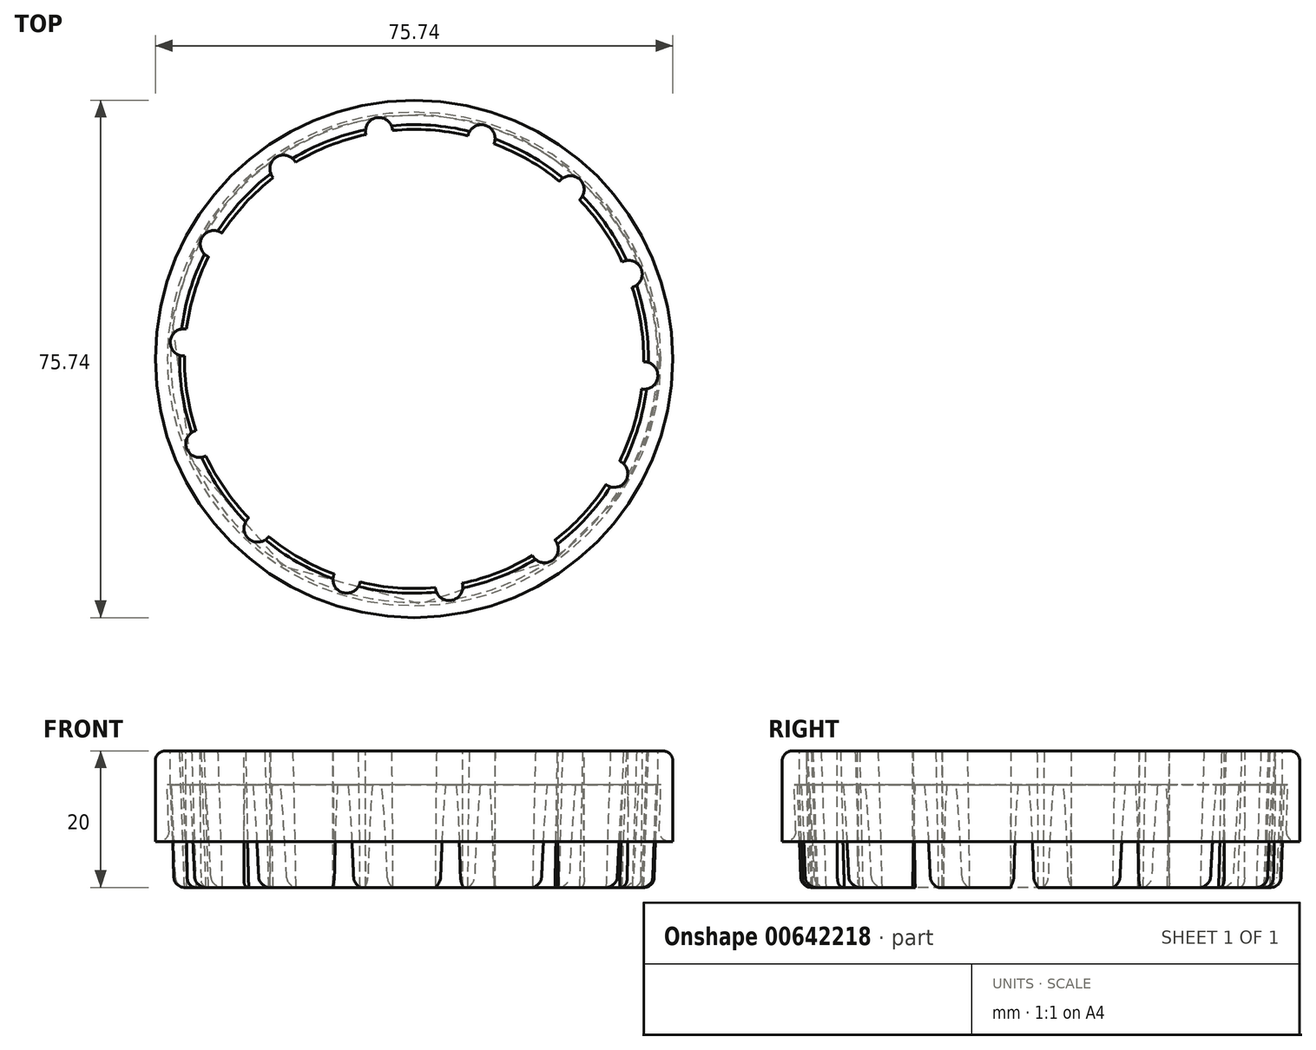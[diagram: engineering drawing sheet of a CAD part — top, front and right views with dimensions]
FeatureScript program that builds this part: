
annotation { "Feature Type Name" : "Feature", "Feature Type Description" : "" }
export const myFeature = defineFeature(function(context is Context, id is Id, definition is map)
    precondition{}
    {
        {
            var Q0;
            Q0=qCreatedBy(makeId("Front.planeOp"),FACE);
            var sketch = newSketch(context, id + "F0", { "sketchPlane" : qUnion([Q0])});
            skLineSegment(sketch, "E0.top", {"start": v(-33.6, 0) * mm, "end": v(-35.1, 0) * mm});
            skLineSegment(sketch, "E1", {"start": v(-35.1, 0) * mm, "end": v(-35.62, 15) * mm});
            skPoint(sketch, "E2.orphan", {"position": v(-35.62, 0) * mm});
            skLineSegment(sketch, "E3.top", {"start": v(-34.3, 20) * mm, "end": v(-37.87, 20) * mm});
            skLineSegment(sketch, "E3.right", {"start": v(-37.87, 15) * mm, "end": v(-37.87, 20) * mm});
            skLineSegment(sketch, "E4", {"start": v(-34.3, 20) * mm, "end": v(-33.6, 0) * mm});
            skLineSegment(sketch, "E5", {"start": v(-36.12, 15) * mm, "end": v(-35.83, 6.78) * mm});
            skLineSegment(sketch, "E6", {"start": v(-37.87, 15) * mm, "end": v(-37.87, 6.71) * mm});
            skLineSegment(sketch, "E7", {"start": v(-35.62, 0) * mm, "end": v(-35.6, 0) * mm});
            skLineSegment(sketch, "E8.trimOffspring", {"start": v(-35.62, 15) * mm, "end": v(-36.12, 15) * mm});
            skPoint(sketch, "E0.left.start.orphan", {"position": v(0, 15) * mm});
            skPoint(sketch, "E9.orphan", {"position": v(0, 0) * mm});
            skLineSegment(sketch, "E10", {"start": v(0, 21.76) * mm, "end": v(0, 0) * mm, "construction": true});
            skLineSegment(sketch, "E11", {"start": v(-35.83, 6.78) * mm, "end": v(-37.87, 6.71) * mm});
            skPoint(sketch, "E12.orphan", {"position": v(-37.87, 0) * mm});
            skSolve(sketch);
        }
        {
            var Q0;
            Q0=makeQuery(id+"F0.imprint","IMPRINT",FACE,{"disambiguationData":[TD([[makeQuery(id+"F0.imprint","IMPRINT",EDGE,{"derivedFrom":sQuery(id+"F0.wireOp",EDGE,"E0.top")}),-1.0]])]});
            var Q1;
            Q1=sQuery(id+"F0.wireOp",EDGE,"E10");
            revolve(context, id + "F1", {"entities" : qUnion([Q0]), "axis" : qUnion([Q1]), "revolveType" : RevolveType.FULL});
        }
        {
            var Q0;
            Q0=makeQuery(id+"F1.opRevolve","SWEPT_FACE",FACE,{"disambiguationData":[OSD([sQuery(id+"F0.wireOp",EDGE,"E3.top")])]});
            var sketch = newSketch(context, id + "F2", { "sketchPlane" : qUnion([Q0])});
            skCircle(sketch, "E13.cCircle", {"center": v(0, 0) * mm, "radius": 32.91 * mm, "construction": true});
            skLineSegment(sketch, "E13.0", {"start": v(-19.1, 27.84) * mm, "end": v(-5.13, 33.37) * mm, "construction": true});
            skLineSegment(sketch, "E13.1", {"start": v(-5.13, 33.37) * mm, "end": v(9.86, 32.29) * mm, "construction": true});
            skLineSegment(sketch, "E13.2", {"start": v(9.86, 32.29) * mm, "end": v(22.9, 24.81) * mm, "construction": true});
            skLineSegment(sketch, "E13.3", {"start": v(22.9, 24.81) * mm, "end": v(31.39, 12.43) * mm, "construction": true});
            skLineSegment(sketch, "E13.4", {"start": v(31.39, 12.43) * mm, "end": v(33.67, -2.42) * mm, "construction": true});
            skLineSegment(sketch, "E13.5", {"start": v(33.67, -2.42) * mm, "end": v(29.29, -16.8) * mm, "construction": true});
            skLineSegment(sketch, "E13.6", {"start": v(29.29, -16.8) * mm, "end": v(19.1, -27.84) * mm, "construction": true});
            skLineSegment(sketch, "E13.7", {"start": v(19.1, -27.84) * mm, "end": v(5.13, -33.37) * mm, "construction": true});
            skLineSegment(sketch, "E13.8", {"start": v(5.13, -33.37) * mm, "end": v(-9.86, -32.29) * mm, "construction": true});
            skLineSegment(sketch, "E13.9", {"start": v(-9.86, -32.29) * mm, "end": v(-22.9, -24.81) * mm, "construction": true});
            skLineSegment(sketch, "E13.10", {"start": v(-22.9, -24.81) * mm, "end": v(-31.39, -12.43) * mm, "construction": true});
            skLineSegment(sketch, "E13.11", {"start": v(-31.39, -12.43) * mm, "end": v(-33.67, 2.42) * mm, "construction": true});
            skLineSegment(sketch, "E13.12", {"start": v(-33.67, 2.42) * mm, "end": v(-29.29, 16.8) * mm, "construction": true});
            skLineSegment(sketch, "E13.13", {"start": v(-29.29, 16.8) * mm, "end": v(-19.1, 27.84) * mm, "construction": true});
            skPoint(sketch, "E13.0.midPoint", {"position": v(-12.11, 30.6) * mm});
            skCircle(sketch, "E14", {"center": v(-5.13, 33.37) * mm, "radius": 1.97 * mm});
            skCircle(sketch, "E15", {"center": v(-19.1, 27.84) * mm, "radius": 2 * mm});
            skCircle(sketch, "E16", {"center": v(-29.29, 16.8) * mm, "radius": 2 * mm});
            skCircle(sketch, "E17", {"center": v(-33.67, 2.42) * mm, "radius": 2 * mm});
            skCircle(sketch, "E18", {"center": v(9.86, 32.29) * mm, "radius": 2 * mm});
            skCircle(sketch, "E19", {"center": v(22.9, 24.81) * mm, "radius": 2 * mm});
            skCircle(sketch, "E20", {"center": v(31.39, 12.43) * mm, "radius": 2 * mm});
            skCircle(sketch, "E21", {"center": v(33.67, -2.42) * mm, "radius": 2 * mm});
            skCircle(sketch, "E22", {"center": v(29.29, -16.8) * mm, "radius": 2 * mm});
            skCircle(sketch, "E23", {"center": v(19.1, -27.84) * mm, "radius": 2 * mm});
            skCircle(sketch, "E24", {"center": v(5.13, -33.37) * mm, "radius": 2 * mm});
            skCircle(sketch, "E25", {"center": v(-9.86, -32.29) * mm, "radius": 2 * mm});
            skCircle(sketch, "E26", {"center": v(-22.9, -24.81) * mm, "radius": 2 * mm});
            skCircle(sketch, "E27", {"center": v(-31.39, -12.43) * mm, "radius": 2 * mm});
            skSolve(sketch);
        }
        {
            var Q0;
            {var subQ0=sQuery(id+"F2.wireOp",EDGE,"E23");var subQ1=makeQuery(id+"F1.opRevolve","SWEPT_EDGE",EDGE,{"disambiguationData":[OSD([sQuery(id+"F0.wireOp",EDGE,"E3.top"),sQuery(id+"F0.wireOp",EDGE,"E4")])]});var subQ2=makeQuery(id+"F2.imprint","INTERSECT",VERTEX,{"disambiguationData":[OD(0.0)],"derivedFrom":[subQ1,subQ0]});Q0=makeQuery(id+"F2.imprint","IMPRINT",FACE,{"disambiguationData":[TD([[makeQuery(id+"F2.imprint","IMPRINT",EDGE,{"disambiguationData":[TD([[subQ2,-1.0]])],"derivedFrom":subQ0}),1.0]])]});}
            var Q1;
            {var subQ0=sQuery(id+"F2.wireOp",EDGE,"E23");var subQ1=makeQuery(id+"F1.opRevolve","SWEPT_EDGE",EDGE,{"disambiguationData":[OSD([sQuery(id+"F0.wireOp",EDGE,"E3.top"),sQuery(id+"F0.wireOp",EDGE,"E4")])]});var subQ2=makeQuery(id+"F2.imprint","INTERSECT",VERTEX,{"disambiguationData":[OD(0.0)],"derivedFrom":[subQ1,subQ0]});Q1=makeQuery(id+"F2.imprint","IMPRINT",FACE,{"disambiguationData":[TD([[makeQuery(id+"F2.imprint","IMPRINT",EDGE,{"disambiguationData":[TD([[subQ2,1.0]])],"derivedFrom":subQ0}),1.0]])]});}
            var Q2;
            {var subQ0=sQuery(id+"F2.wireOp",EDGE,"E22");var subQ1=makeQuery(id+"F1.opRevolve","SWEPT_EDGE",EDGE,{"disambiguationData":[OSD([sQuery(id+"F0.wireOp",EDGE,"E3.top"),sQuery(id+"F0.wireOp",EDGE,"E4")])]});var subQ2=makeQuery(id+"F2.imprint","INTERSECT",VERTEX,{"disambiguationData":[OD(0.0)],"derivedFrom":[subQ1,subQ0]});Q2=makeQuery(id+"F2.imprint","IMPRINT",FACE,{"disambiguationData":[TD([[makeQuery(id+"F2.imprint","IMPRINT",EDGE,{"disambiguationData":[TD([[subQ2,-1.0]])],"derivedFrom":subQ0}),1.0]])]});}
            var Q3;
            {var subQ0=sQuery(id+"F2.wireOp",EDGE,"E21");var subQ1=makeQuery(id+"F1.opRevolve","SWEPT_EDGE",EDGE,{"disambiguationData":[OSD([sQuery(id+"F0.wireOp",EDGE,"E3.top"),sQuery(id+"F0.wireOp",EDGE,"E4")])]});var subQ2=makeQuery(id+"F2.imprint","INTERSECT",VERTEX,{"disambiguationData":[OD(0.0)],"derivedFrom":[subQ1,subQ0]});Q3=makeQuery(id+"F2.imprint","IMPRINT",FACE,{"disambiguationData":[TD([[makeQuery(id+"F2.imprint","IMPRINT",EDGE,{"disambiguationData":[TD([[subQ2,-1.0]])],"derivedFrom":subQ0}),1.0]])]});}
            var Q4;
            {var subQ0=sQuery(id+"F2.wireOp",EDGE,"E20");var subQ1=makeQuery(id+"F1.opRevolve","SWEPT_EDGE",EDGE,{"disambiguationData":[OSD([sQuery(id+"F0.wireOp",EDGE,"E3.top"),sQuery(id+"F0.wireOp",EDGE,"E4")])]});var subQ2=makeQuery(id+"F2.imprint","INTERSECT",VERTEX,{"disambiguationData":[OD(0.0)],"derivedFrom":[subQ1,subQ0]});Q4=makeQuery(id+"F2.imprint","IMPRINT",FACE,{"disambiguationData":[TD([[makeQuery(id+"F2.imprint","IMPRINT",EDGE,{"disambiguationData":[TD([[subQ2,-1.0]])],"derivedFrom":subQ0}),1.0]])]});}
            var Q5;
            {var subQ0=sQuery(id+"F2.wireOp",EDGE,"E20");var subQ1=makeQuery(id+"F1.opRevolve","SWEPT_EDGE",EDGE,{"disambiguationData":[OSD([sQuery(id+"F0.wireOp",EDGE,"E3.top"),sQuery(id+"F0.wireOp",EDGE,"E4")])]});var subQ2=makeQuery(id+"F2.imprint","INTERSECT",VERTEX,{"disambiguationData":[OD(0.0)],"derivedFrom":[subQ1,subQ0]});Q5=makeQuery(id+"F2.imprint","IMPRINT",FACE,{"disambiguationData":[TD([[makeQuery(id+"F2.imprint","IMPRINT",EDGE,{"disambiguationData":[TD([[subQ2,1.0]])],"derivedFrom":subQ0}),1.0]])]});}
            var Q6;
            {var subQ0=sQuery(id+"F2.wireOp",EDGE,"E21");var subQ1=makeQuery(id+"F1.opRevolve","SWEPT_EDGE",EDGE,{"disambiguationData":[OSD([sQuery(id+"F0.wireOp",EDGE,"E3.top"),sQuery(id+"F0.wireOp",EDGE,"E4")])]});var subQ2=makeQuery(id+"F2.imprint","INTERSECT",VERTEX,{"disambiguationData":[OD(0.0)],"derivedFrom":[subQ1,subQ0]});Q6=makeQuery(id+"F2.imprint","IMPRINT",FACE,{"disambiguationData":[TD([[makeQuery(id+"F2.imprint","IMPRINT",EDGE,{"disambiguationData":[TD([[subQ2,1.0]])],"derivedFrom":subQ0}),1.0]])]});}
            var Q7;
            {var subQ0=sQuery(id+"F2.wireOp",EDGE,"E19");var subQ1=makeQuery(id+"F1.opRevolve","SWEPT_EDGE",EDGE,{"disambiguationData":[OSD([sQuery(id+"F0.wireOp",EDGE,"E3.top"),sQuery(id+"F0.wireOp",EDGE,"E4")])]});var subQ2=makeQuery(id+"F2.imprint","INTERSECT",VERTEX,{"disambiguationData":[OD(0.0)],"derivedFrom":[subQ1,subQ0]});Q7=makeQuery(id+"F2.imprint","IMPRINT",FACE,{"disambiguationData":[TD([[makeQuery(id+"F2.imprint","IMPRINT",EDGE,{"disambiguationData":[TD([[subQ2,1.0]])],"derivedFrom":subQ0}),1.0]])]});}
            var Q8;
            {var subQ0=sQuery(id+"F2.wireOp",EDGE,"E18");var subQ1=makeQuery(id+"F1.opRevolve","SWEPT_EDGE",EDGE,{"disambiguationData":[OSD([sQuery(id+"F0.wireOp",EDGE,"E3.top"),sQuery(id+"F0.wireOp",EDGE,"E4")])]});var subQ2=makeQuery(id+"F2.imprint","INTERSECT",VERTEX,{"disambiguationData":[OD(0.0)],"derivedFrom":[subQ1,subQ0]});Q8=makeQuery(id+"F2.imprint","IMPRINT",FACE,{"disambiguationData":[TD([[makeQuery(id+"F2.imprint","IMPRINT",EDGE,{"disambiguationData":[TD([[subQ2,1.0]])],"derivedFrom":subQ0}),1.0]])]});}
            var Q9;
            {var subQ0=sQuery(id+"F2.wireOp",EDGE,"E18");var subQ1=makeQuery(id+"F1.opRevolve","SWEPT_EDGE",EDGE,{"disambiguationData":[OSD([sQuery(id+"F0.wireOp",EDGE,"E3.top"),sQuery(id+"F0.wireOp",EDGE,"E4")])]});var subQ2=makeQuery(id+"F2.imprint","INTERSECT",VERTEX,{"disambiguationData":[OD(0.0)],"derivedFrom":[subQ1,subQ0]});Q9=makeQuery(id+"F2.imprint","IMPRINT",FACE,{"disambiguationData":[TD([[makeQuery(id+"F2.imprint","IMPRINT",EDGE,{"disambiguationData":[TD([[subQ2,-1.0]])],"derivedFrom":subQ0}),1.0]])]});}
            var Q10;
            {var subQ0=sQuery(id+"F2.wireOp",EDGE,"E14");var subQ1=makeQuery(id+"F1.opRevolve","SWEPT_EDGE",EDGE,{"disambiguationData":[OSD([sQuery(id+"F0.wireOp",EDGE,"E3.top"),sQuery(id+"F0.wireOp",EDGE,"E4")])]});var subQ2=makeQuery(id+"F2.imprint","INTERSECT",VERTEX,{"disambiguationData":[OD(0.0)],"derivedFrom":[subQ1,subQ0]});Q10=makeQuery(id+"F2.imprint","IMPRINT",FACE,{"disambiguationData":[TD([[makeQuery(id+"F2.imprint","IMPRINT",EDGE,{"disambiguationData":[TD([[subQ2,1.0]])],"derivedFrom":subQ0}),1.0]])]});}
            var Q11;
            {var subQ0=sQuery(id+"F2.wireOp",EDGE,"E15");var subQ1=makeQuery(id+"F1.opRevolve","SWEPT_EDGE",EDGE,{"disambiguationData":[OSD([sQuery(id+"F0.wireOp",EDGE,"E3.top"),sQuery(id+"F0.wireOp",EDGE,"E4")])]});var subQ2=makeQuery(id+"F2.imprint","INTERSECT",VERTEX,{"disambiguationData":[OD(0.0)],"derivedFrom":[subQ1,subQ0]});Q11=makeQuery(id+"F2.imprint","IMPRINT",FACE,{"disambiguationData":[TD([[makeQuery(id+"F2.imprint","IMPRINT",EDGE,{"disambiguationData":[TD([[subQ2,1.0]])],"derivedFrom":subQ0}),1.0]])]});}
            var Q12;
            {var subQ0=sQuery(id+"F2.wireOp",EDGE,"E16");var subQ1=makeQuery(id+"F1.opRevolve","SWEPT_EDGE",EDGE,{"disambiguationData":[OSD([sQuery(id+"F0.wireOp",EDGE,"E3.top"),sQuery(id+"F0.wireOp",EDGE,"E4")])]});var subQ2=makeQuery(id+"F2.imprint","INTERSECT",VERTEX,{"disambiguationData":[OD(0.0)],"derivedFrom":[subQ1,subQ0]});Q12=makeQuery(id+"F2.imprint","IMPRINT",FACE,{"disambiguationData":[TD([[makeQuery(id+"F2.imprint","IMPRINT",EDGE,{"disambiguationData":[TD([[subQ2,1.0]])],"derivedFrom":subQ0}),1.0]])]});}
            var Q13;
            {var subQ0=sQuery(id+"F2.wireOp",EDGE,"E17");var subQ1=makeQuery(id+"F1.opRevolve","SWEPT_EDGE",EDGE,{"disambiguationData":[OSD([sQuery(id+"F0.wireOp",EDGE,"E3.top"),sQuery(id+"F0.wireOp",EDGE,"E4")])]});var subQ2=makeQuery(id+"F2.imprint","INTERSECT",VERTEX,{"disambiguationData":[OD(0.0)],"derivedFrom":[subQ1,subQ0]});Q13=makeQuery(id+"F2.imprint","IMPRINT",FACE,{"disambiguationData":[TD([[makeQuery(id+"F2.imprint","IMPRINT",EDGE,{"disambiguationData":[TD([[subQ2,1.0]])],"derivedFrom":subQ0}),1.0]])]});}
            var Q14;
            {var subQ0=sQuery(id+"F2.wireOp",EDGE,"E24");var subQ1=makeQuery(id+"F1.opRevolve","SWEPT_EDGE",EDGE,{"disambiguationData":[OSD([sQuery(id+"F0.wireOp",EDGE,"E3.top"),sQuery(id+"F0.wireOp",EDGE,"E4")])]});var subQ2=makeQuery(id+"F2.imprint","INTERSECT",VERTEX,{"disambiguationData":[OD(0.0)],"derivedFrom":[subQ1,subQ0]});Q14=makeQuery(id+"F2.imprint","IMPRINT",FACE,{"disambiguationData":[TD([[makeQuery(id+"F2.imprint","IMPRINT",EDGE,{"disambiguationData":[TD([[subQ2,-1.0]])],"derivedFrom":subQ0}),1.0]])]});}
            var Q15;
            {var subQ0=sQuery(id+"F2.wireOp",EDGE,"E24");var subQ1=makeQuery(id+"F1.opRevolve","SWEPT_EDGE",EDGE,{"disambiguationData":[OSD([sQuery(id+"F0.wireOp",EDGE,"E3.top"),sQuery(id+"F0.wireOp",EDGE,"E4")])]});var subQ2=makeQuery(id+"F2.imprint","INTERSECT",VERTEX,{"disambiguationData":[OD(0.0)],"derivedFrom":[subQ1,subQ0]});Q15=makeQuery(id+"F2.imprint","IMPRINT",FACE,{"disambiguationData":[TD([[makeQuery(id+"F2.imprint","IMPRINT",EDGE,{"disambiguationData":[TD([[subQ2,1.0]])],"derivedFrom":subQ0}),1.0]])]});}
            var Q16;
            {var subQ0=sQuery(id+"F2.wireOp",EDGE,"E19");var subQ1=makeQuery(id+"F1.opRevolve","SWEPT_EDGE",EDGE,{"disambiguationData":[OSD([sQuery(id+"F0.wireOp",EDGE,"E3.top"),sQuery(id+"F0.wireOp",EDGE,"E4")])]});var subQ2=makeQuery(id+"F2.imprint","INTERSECT",VERTEX,{"disambiguationData":[OD(0.0)],"derivedFrom":[subQ1,subQ0]});Q16=makeQuery(id+"F2.imprint","IMPRINT",FACE,{"disambiguationData":[TD([[makeQuery(id+"F2.imprint","IMPRINT",EDGE,{"disambiguationData":[TD([[subQ2,-1.0]])],"derivedFrom":subQ0}),1.0]])]});}
            var Q17;
            {var subQ0=sQuery(id+"F2.wireOp",EDGE,"E14");var subQ1=makeQuery(id+"F1.opRevolve","SWEPT_EDGE",EDGE,{"disambiguationData":[OSD([sQuery(id+"F0.wireOp",EDGE,"E3.top"),sQuery(id+"F0.wireOp",EDGE,"E4")])]});var subQ2=makeQuery(id+"F2.imprint","INTERSECT",VERTEX,{"disambiguationData":[OD(0.0)],"derivedFrom":[subQ1,subQ0]});Q17=makeQuery(id+"F2.imprint","IMPRINT",FACE,{"disambiguationData":[TD([[makeQuery(id+"F2.imprint","IMPRINT",EDGE,{"disambiguationData":[TD([[subQ2,-1.0]])],"derivedFrom":subQ0}),1.0]])]});}
            var Q18;
            {var subQ0=sQuery(id+"F2.wireOp",EDGE,"E15");var subQ1=makeQuery(id+"F1.opRevolve","SWEPT_EDGE",EDGE,{"disambiguationData":[OSD([sQuery(id+"F0.wireOp",EDGE,"E3.top"),sQuery(id+"F0.wireOp",EDGE,"E4")])]});var subQ2=makeQuery(id+"F2.imprint","INTERSECT",VERTEX,{"disambiguationData":[OD(0.0)],"derivedFrom":[subQ1,subQ0]});Q18=makeQuery(id+"F2.imprint","IMPRINT",FACE,{"disambiguationData":[TD([[makeQuery(id+"F2.imprint","IMPRINT",EDGE,{"disambiguationData":[TD([[subQ2,-1.0]])],"derivedFrom":subQ0}),1.0]])]});}
            var Q19;
            {var subQ0=sQuery(id+"F2.wireOp",EDGE,"E16");var subQ1=makeQuery(id+"F1.opRevolve","SWEPT_EDGE",EDGE,{"disambiguationData":[OSD([sQuery(id+"F0.wireOp",EDGE,"E3.top"),sQuery(id+"F0.wireOp",EDGE,"E4")])]});var subQ2=makeQuery(id+"F2.imprint","INTERSECT",VERTEX,{"disambiguationData":[OD(0.0)],"derivedFrom":[subQ1,subQ0]});Q19=makeQuery(id+"F2.imprint","IMPRINT",FACE,{"disambiguationData":[TD([[makeQuery(id+"F2.imprint","IMPRINT",EDGE,{"disambiguationData":[TD([[subQ2,-1.0]])],"derivedFrom":subQ0}),1.0]])]});}
            var Q20;
            {var subQ0=sQuery(id+"F2.wireOp",EDGE,"E22");var subQ1=makeQuery(id+"F1.opRevolve","SWEPT_EDGE",EDGE,{"disambiguationData":[OSD([sQuery(id+"F0.wireOp",EDGE,"E3.top"),sQuery(id+"F0.wireOp",EDGE,"E4")])]});var subQ2=makeQuery(id+"F2.imprint","INTERSECT",VERTEX,{"disambiguationData":[OD(0.0)],"derivedFrom":[subQ1,subQ0]});Q20=makeQuery(id+"F2.imprint","IMPRINT",FACE,{"disambiguationData":[TD([[makeQuery(id+"F2.imprint","IMPRINT",EDGE,{"disambiguationData":[TD([[subQ2,1.0]])],"derivedFrom":subQ0}),1.0]])]});}
            var Q21;
            {var subQ0=sQuery(id+"F2.wireOp",EDGE,"E25");var subQ1=makeQuery(id+"F1.opRevolve","SWEPT_EDGE",EDGE,{"disambiguationData":[OSD([sQuery(id+"F0.wireOp",EDGE,"E3.top"),sQuery(id+"F0.wireOp",EDGE,"E4")])]});var subQ2=makeQuery(id+"F2.imprint","INTERSECT",VERTEX,{"disambiguationData":[OD(0.0)],"derivedFrom":[subQ1,subQ0]});Q21=makeQuery(id+"F2.imprint","IMPRINT",FACE,{"disambiguationData":[TD([[makeQuery(id+"F2.imprint","IMPRINT",EDGE,{"disambiguationData":[TD([[subQ2,-1.0]])],"derivedFrom":subQ0}),1.0]])]});}
            var Q22;
            {var subQ0=sQuery(id+"F2.wireOp",EDGE,"E26");var subQ1=makeQuery(id+"F1.opRevolve","SWEPT_EDGE",EDGE,{"disambiguationData":[OSD([sQuery(id+"F0.wireOp",EDGE,"E3.top"),sQuery(id+"F0.wireOp",EDGE,"E4")])]});var subQ2=makeQuery(id+"F2.imprint","INTERSECT",VERTEX,{"disambiguationData":[OD(0.0)],"derivedFrom":[subQ1,subQ0]});Q22=makeQuery(id+"F2.imprint","IMPRINT",FACE,{"disambiguationData":[TD([[makeQuery(id+"F2.imprint","IMPRINT",EDGE,{"disambiguationData":[TD([[subQ2,-1.0]])],"derivedFrom":subQ0}),1.0]])]});}
            var Q23;
            {var subQ0=sQuery(id+"F2.wireOp",EDGE,"E27");var subQ1=makeQuery(id+"F1.opRevolve","SWEPT_EDGE",EDGE,{"disambiguationData":[OSD([sQuery(id+"F0.wireOp",EDGE,"E3.top"),sQuery(id+"F0.wireOp",EDGE,"E4")])]});var subQ2=makeQuery(id+"F2.imprint","INTERSECT",VERTEX,{"disambiguationData":[OD(0.0)],"derivedFrom":[subQ1,subQ0]});Q23=makeQuery(id+"F2.imprint","IMPRINT",FACE,{"disambiguationData":[TD([[makeQuery(id+"F2.imprint","IMPRINT",EDGE,{"disambiguationData":[TD([[subQ2,1.0]])],"derivedFrom":subQ0}),1.0]])]});}
            var Q24;
            {var subQ0=sQuery(id+"F2.wireOp",EDGE,"E26");var subQ1=makeQuery(id+"F1.opRevolve","SWEPT_EDGE",EDGE,{"disambiguationData":[OSD([sQuery(id+"F0.wireOp",EDGE,"E3.top"),sQuery(id+"F0.wireOp",EDGE,"E4")])]});var subQ2=makeQuery(id+"F2.imprint","INTERSECT",VERTEX,{"disambiguationData":[OD(0.0)],"derivedFrom":[subQ1,subQ0]});Q24=makeQuery(id+"F2.imprint","IMPRINT",FACE,{"disambiguationData":[TD([[makeQuery(id+"F2.imprint","IMPRINT",EDGE,{"disambiguationData":[TD([[subQ2,1.0]])],"derivedFrom":subQ0}),1.0]])]});}
            var Q25;
            {var subQ0=sQuery(id+"F2.wireOp",EDGE,"E25");var subQ1=makeQuery(id+"F1.opRevolve","SWEPT_EDGE",EDGE,{"disambiguationData":[OSD([sQuery(id+"F0.wireOp",EDGE,"E3.top"),sQuery(id+"F0.wireOp",EDGE,"E4")])]});var subQ2=makeQuery(id+"F2.imprint","INTERSECT",VERTEX,{"disambiguationData":[OD(0.0)],"derivedFrom":[subQ1,subQ0]});Q25=makeQuery(id+"F2.imprint","IMPRINT",FACE,{"disambiguationData":[TD([[makeQuery(id+"F2.imprint","IMPRINT",EDGE,{"disambiguationData":[TD([[subQ2,1.0]])],"derivedFrom":subQ0}),1.0]])]});}
            var Q26;
            {var subQ0=sQuery(id+"F2.wireOp",EDGE,"E27");var subQ1=makeQuery(id+"F1.opRevolve","SWEPT_EDGE",EDGE,{"disambiguationData":[OSD([sQuery(id+"F0.wireOp",EDGE,"E3.top"),sQuery(id+"F0.wireOp",EDGE,"E4")])]});var subQ2=makeQuery(id+"F2.imprint","INTERSECT",VERTEX,{"disambiguationData":[OD(0.0)],"derivedFrom":[subQ1,subQ0]});Q26=makeQuery(id+"F2.imprint","IMPRINT",FACE,{"disambiguationData":[TD([[makeQuery(id+"F2.imprint","IMPRINT",EDGE,{"disambiguationData":[TD([[subQ2,-1.0]])],"derivedFrom":subQ0}),1.0]])]});}
            var Q27;
            {var subQ0=sQuery(id+"F2.wireOp",EDGE,"E17");var subQ1=makeQuery(id+"F1.opRevolve","SWEPT_EDGE",EDGE,{"disambiguationData":[OSD([sQuery(id+"F0.wireOp",EDGE,"E3.top"),sQuery(id+"F0.wireOp",EDGE,"E4")])]});var subQ2=makeQuery(id+"F2.imprint","INTERSECT",VERTEX,{"disambiguationData":[OD(0.0)],"derivedFrom":[subQ1,subQ0]});Q27=makeQuery(id+"F2.imprint","IMPRINT",FACE,{"disambiguationData":[TD([[makeQuery(id+"F2.imprint","IMPRINT",EDGE,{"disambiguationData":[TD([[subQ2,-1.0]])],"derivedFrom":subQ0}),1.0]])]});}
            extrude(context, id + "F3", {"entities" : qUnion([Q0, Q1, Q2, Q3, Q4, Q5, Q6, Q7, Q8, Q9, Q10, Q11, Q12, Q13, Q14, Q15, Q16, Q17, Q18, Q19, Q20, Q21, Q22, Q23, Q24, Q25, Q26, Q27]), "operationType" : NewBodyOperationType.REMOVE, "oppositeDirection" : true, "depth" : 25 * mm, "offsetDistance" : 25 * mm});
        }
        {
            var Q0;
            {var subQ0=sQuery(id+"F0.wireOp",EDGE,"E0.top");var subQ1=sQuery(id+"F0.wireOp",EDGE,"E1");Q0=makeQuery(id+"F3.boolean.opBoolean","SPLIT",EDGE,{"disambiguationData":[TD([makeQuery(id+"F1.opRevolve","SWEPT_FACE",FACE,{"disambiguationData":[OSD([subQ0])]}),makeQuery(id+"F1.opRevolve","SWEPT_FACE",FACE,{"disambiguationData":[OSD([subQ1])]}),makeQuery(id+"F3.opExtrude","SWEPT_FACE",FACE,{"disambiguationData":[OSD([sQuery(id+"F2.wireOp",EDGE,"E26")])]}),makeQuery(id+"F3.opExtrude","SWEPT_FACE",FACE,{"disambiguationData":[OSD([sQuery(id+"F2.wireOp",EDGE,"E27")])]})])],"derivedFrom":makeQuery(id+"F1.opRevolve","SWEPT_EDGE",EDGE,{"disambiguationData":[OSD([subQ0,subQ1])]})});}
            var Q1;
            {var subQ0=sQuery(id+"F0.wireOp",EDGE,"E0.top");var subQ1=sQuery(id+"F0.wireOp",EDGE,"E1");Q1=makeQuery(id+"F3.boolean.opBoolean","SPLIT",EDGE,{"disambiguationData":[TD([makeQuery(id+"F1.opRevolve","SWEPT_FACE",FACE,{"disambiguationData":[OSD([subQ0])]}),makeQuery(id+"F1.opRevolve","SWEPT_FACE",FACE,{"disambiguationData":[OSD([subQ1])]}),makeQuery(id+"F3.opExtrude","SWEPT_FACE",FACE,{"disambiguationData":[OSD([sQuery(id+"F2.wireOp",EDGE,"E25")])]}),makeQuery(id+"F3.opExtrude","SWEPT_FACE",FACE,{"disambiguationData":[OSD([sQuery(id+"F2.wireOp",EDGE,"E26")])]})])],"derivedFrom":makeQuery(id+"F1.opRevolve","SWEPT_EDGE",EDGE,{"disambiguationData":[OSD([subQ0,subQ1])]})});}
            var Q2;
            {var subQ0=sQuery(id+"F0.wireOp",EDGE,"E0.top");var subQ1=sQuery(id+"F0.wireOp",EDGE,"E1");Q2=makeQuery(id+"F3.boolean.opBoolean","SPLIT",EDGE,{"disambiguationData":[TD([makeQuery(id+"F1.opRevolve","SWEPT_FACE",FACE,{"disambiguationData":[OSD([subQ0])]}),makeQuery(id+"F1.opRevolve","SWEPT_FACE",FACE,{"disambiguationData":[OSD([subQ1])]}),makeQuery(id+"F3.opExtrude","SWEPT_FACE",FACE,{"disambiguationData":[OSD([sQuery(id+"F2.wireOp",EDGE,"E24")])]}),makeQuery(id+"F3.opExtrude","SWEPT_FACE",FACE,{"disambiguationData":[OSD([sQuery(id+"F2.wireOp",EDGE,"E25")])]})])],"derivedFrom":makeQuery(id+"F1.opRevolve","SWEPT_EDGE",EDGE,{"disambiguationData":[OSD([subQ0,subQ1])]})});}
            var Q3;
            {var subQ0=sQuery(id+"F0.wireOp",EDGE,"E0.top");var subQ1=sQuery(id+"F0.wireOp",EDGE,"E1");Q3=makeQuery(id+"F3.boolean.opBoolean","SPLIT",EDGE,{"disambiguationData":[TD([makeQuery(id+"F1.opRevolve","SWEPT_FACE",FACE,{"disambiguationData":[OSD([subQ0])]}),makeQuery(id+"F1.opRevolve","SWEPT_FACE",FACE,{"disambiguationData":[OSD([subQ1])]}),makeQuery(id+"F3.opExtrude","SWEPT_FACE",FACE,{"disambiguationData":[OSD([sQuery(id+"F2.wireOp",EDGE,"E23")])]}),makeQuery(id+"F3.opExtrude","SWEPT_FACE",FACE,{"disambiguationData":[OSD([sQuery(id+"F2.wireOp",EDGE,"E24")])]})])],"derivedFrom":makeQuery(id+"F1.opRevolve","SWEPT_EDGE",EDGE,{"disambiguationData":[OSD([subQ0,subQ1])]})});}
            var Q4;
            {var subQ0=sQuery(id+"F0.wireOp",EDGE,"E0.top");var subQ1=sQuery(id+"F0.wireOp",EDGE,"E1");Q4=makeQuery(id+"F3.boolean.opBoolean","SPLIT",EDGE,{"disambiguationData":[TD([makeQuery(id+"F1.opRevolve","SWEPT_FACE",FACE,{"disambiguationData":[OSD([subQ0])]}),makeQuery(id+"F1.opRevolve","SWEPT_FACE",FACE,{"disambiguationData":[OSD([subQ1])]}),makeQuery(id+"F3.opExtrude","SWEPT_FACE",FACE,{"disambiguationData":[OSD([sQuery(id+"F2.wireOp",EDGE,"E22")])]}),makeQuery(id+"F3.opExtrude","SWEPT_FACE",FACE,{"disambiguationData":[OSD([sQuery(id+"F2.wireOp",EDGE,"E23")])]})])],"derivedFrom":makeQuery(id+"F1.opRevolve","SWEPT_EDGE",EDGE,{"disambiguationData":[OSD([subQ0,subQ1])]})});}
            var Q5;
            {var subQ0=sQuery(id+"F0.wireOp",EDGE,"E0.top");var subQ1=sQuery(id+"F0.wireOp",EDGE,"E1");Q5=makeQuery(id+"F3.boolean.opBoolean","SPLIT",EDGE,{"disambiguationData":[TD([makeQuery(id+"F1.opRevolve","SWEPT_FACE",FACE,{"disambiguationData":[OSD([subQ0])]}),makeQuery(id+"F1.opRevolve","SWEPT_FACE",FACE,{"disambiguationData":[OSD([subQ1])]}),makeQuery(id+"F3.opExtrude","SWEPT_FACE",FACE,{"disambiguationData":[OSD([sQuery(id+"F2.wireOp",EDGE,"E21")])]}),makeQuery(id+"F3.opExtrude","SWEPT_FACE",FACE,{"disambiguationData":[OSD([sQuery(id+"F2.wireOp",EDGE,"E22")])]})])],"derivedFrom":makeQuery(id+"F1.opRevolve","SWEPT_EDGE",EDGE,{"disambiguationData":[OSD([subQ0,subQ1])]})});}
            var Q6;
            {var subQ0=sQuery(id+"F0.wireOp",EDGE,"E0.top");var subQ1=sQuery(id+"F0.wireOp",EDGE,"E1");Q6=makeQuery(id+"F3.boolean.opBoolean","SPLIT",EDGE,{"disambiguationData":[TD([makeQuery(id+"F1.opRevolve","SWEPT_FACE",FACE,{"disambiguationData":[OSD([subQ0])]}),makeQuery(id+"F1.opRevolve","SWEPT_FACE",FACE,{"disambiguationData":[OSD([subQ1])]}),makeQuery(id+"F3.opExtrude","SWEPT_FACE",FACE,{"disambiguationData":[OSD([sQuery(id+"F2.wireOp",EDGE,"E20")])]}),makeQuery(id+"F3.opExtrude","SWEPT_FACE",FACE,{"disambiguationData":[OSD([sQuery(id+"F2.wireOp",EDGE,"E21")])]})])],"derivedFrom":makeQuery(id+"F1.opRevolve","SWEPT_EDGE",EDGE,{"disambiguationData":[OSD([subQ0,subQ1])]})});}
            var Q7;
            {var subQ0=sQuery(id+"F0.wireOp",EDGE,"E0.top");var subQ1=sQuery(id+"F0.wireOp",EDGE,"E1");Q7=makeQuery(id+"F3.boolean.opBoolean","SPLIT",EDGE,{"disambiguationData":[TD([makeQuery(id+"F1.opRevolve","SWEPT_FACE",FACE,{"disambiguationData":[OSD([subQ0])]}),makeQuery(id+"F1.opRevolve","SWEPT_FACE",FACE,{"disambiguationData":[OSD([subQ1])]}),makeQuery(id+"F3.opExtrude","SWEPT_FACE",FACE,{"disambiguationData":[OSD([sQuery(id+"F2.wireOp",EDGE,"E19")])]}),makeQuery(id+"F3.opExtrude","SWEPT_FACE",FACE,{"disambiguationData":[OSD([sQuery(id+"F2.wireOp",EDGE,"E20")])]})])],"derivedFrom":makeQuery(id+"F1.opRevolve","SWEPT_EDGE",EDGE,{"disambiguationData":[OSD([subQ0,subQ1])]})});}
            var Q8;
            {var subQ0=sQuery(id+"F0.wireOp",EDGE,"E0.top");var subQ1=sQuery(id+"F0.wireOp",EDGE,"E1");Q8=makeQuery(id+"F3.boolean.opBoolean","SPLIT",EDGE,{"disambiguationData":[TD([makeQuery(id+"F1.opRevolve","SWEPT_FACE",FACE,{"disambiguationData":[OSD([subQ0])]}),makeQuery(id+"F1.opRevolve","SWEPT_FACE",FACE,{"disambiguationData":[OSD([subQ1])]}),makeQuery(id+"F3.opExtrude","SWEPT_FACE",FACE,{"disambiguationData":[OSD([sQuery(id+"F2.wireOp",EDGE,"E18")])]}),makeQuery(id+"F3.opExtrude","SWEPT_FACE",FACE,{"disambiguationData":[OSD([sQuery(id+"F2.wireOp",EDGE,"E19")])]})])],"derivedFrom":makeQuery(id+"F1.opRevolve","SWEPT_EDGE",EDGE,{"disambiguationData":[OSD([subQ0,subQ1])]})});}
            var Q9;
            {var subQ0=sQuery(id+"F0.wireOp",EDGE,"E0.top");var subQ1=sQuery(id+"F0.wireOp",EDGE,"E1");Q9=makeQuery(id+"F3.boolean.opBoolean","SPLIT",EDGE,{"disambiguationData":[TD([makeQuery(id+"F1.opRevolve","SWEPT_FACE",FACE,{"disambiguationData":[OSD([subQ0])]}),makeQuery(id+"F1.opRevolve","SWEPT_FACE",FACE,{"disambiguationData":[OSD([subQ1])]}),makeQuery(id+"F3.opExtrude","SWEPT_FACE",FACE,{"disambiguationData":[OSD([sQuery(id+"F2.wireOp",EDGE,"E14")])]}),makeQuery(id+"F3.opExtrude","SWEPT_FACE",FACE,{"disambiguationData":[OSD([sQuery(id+"F2.wireOp",EDGE,"E18")])]})])],"derivedFrom":makeQuery(id+"F1.opRevolve","SWEPT_EDGE",EDGE,{"disambiguationData":[OSD([subQ0,subQ1])]})});}
            var Q10;
            {var subQ0=sQuery(id+"F0.wireOp",EDGE,"E0.top");var subQ1=sQuery(id+"F0.wireOp",EDGE,"E1");Q10=makeQuery(id+"F3.boolean.opBoolean","SPLIT",EDGE,{"disambiguationData":[TD([makeQuery(id+"F1.opRevolve","SWEPT_FACE",FACE,{"disambiguationData":[OSD([subQ0])]}),makeQuery(id+"F1.opRevolve","SWEPT_FACE",FACE,{"disambiguationData":[OSD([subQ1])]}),makeQuery(id+"F3.opExtrude","SWEPT_FACE",FACE,{"disambiguationData":[OSD([sQuery(id+"F2.wireOp",EDGE,"E14")])]}),makeQuery(id+"F3.opExtrude","SWEPT_FACE",FACE,{"disambiguationData":[OSD([sQuery(id+"F2.wireOp",EDGE,"E15")])]})])],"derivedFrom":makeQuery(id+"F1.opRevolve","SWEPT_EDGE",EDGE,{"disambiguationData":[OSD([subQ0,subQ1])]})});}
            var Q11;
            {var subQ0=sQuery(id+"F0.wireOp",EDGE,"E0.top");var subQ1=sQuery(id+"F0.wireOp",EDGE,"E1");Q11=makeQuery(id+"F3.boolean.opBoolean","SPLIT",EDGE,{"disambiguationData":[TD([makeQuery(id+"F1.opRevolve","SWEPT_FACE",FACE,{"disambiguationData":[OSD([subQ0])]}),makeQuery(id+"F1.opRevolve","SWEPT_FACE",FACE,{"disambiguationData":[OSD([subQ1])]}),makeQuery(id+"F3.opExtrude","SWEPT_FACE",FACE,{"disambiguationData":[OSD([sQuery(id+"F2.wireOp",EDGE,"E16")])]}),makeQuery(id+"F3.opExtrude","SWEPT_FACE",FACE,{"disambiguationData":[OSD([sQuery(id+"F2.wireOp",EDGE,"E17")])]})])],"derivedFrom":makeQuery(id+"F1.opRevolve","SWEPT_EDGE",EDGE,{"disambiguationData":[OSD([subQ0,subQ1])]})});}
            var Q12;
            {var subQ0=sQuery(id+"F0.wireOp",EDGE,"E0.top");var subQ1=sQuery(id+"F0.wireOp",EDGE,"E1");Q12=makeQuery(id+"F3.boolean.opBoolean","SPLIT",EDGE,{"disambiguationData":[TD([makeQuery(id+"F1.opRevolve","SWEPT_FACE",FACE,{"disambiguationData":[OSD([subQ0])]}),makeQuery(id+"F1.opRevolve","SWEPT_FACE",FACE,{"disambiguationData":[OSD([subQ1])]}),makeQuery(id+"F3.opExtrude","SWEPT_FACE",FACE,{"disambiguationData":[OSD([sQuery(id+"F2.wireOp",EDGE,"E17")])]}),makeQuery(id+"F3.opExtrude","SWEPT_FACE",FACE,{"disambiguationData":[OSD([sQuery(id+"F2.wireOp",EDGE,"E27")])]})])],"derivedFrom":makeQuery(id+"F1.opRevolve","SWEPT_EDGE",EDGE,{"disambiguationData":[OSD([subQ0,subQ1])]})});}
            var Q13;
            {var subQ0=sQuery(id+"F0.wireOp",EDGE,"E0.top");var subQ1=sQuery(id+"F0.wireOp",EDGE,"E1");Q13=makeQuery(id+"F3.boolean.opBoolean","SPLIT",EDGE,{"disambiguationData":[TD([makeQuery(id+"F1.opRevolve","SWEPT_FACE",FACE,{"disambiguationData":[OSD([subQ0])]}),makeQuery(id+"F1.opRevolve","SWEPT_FACE",FACE,{"disambiguationData":[OSD([subQ1])]}),makeQuery(id+"F3.opExtrude","SWEPT_FACE",FACE,{"disambiguationData":[OSD([sQuery(id+"F2.wireOp",EDGE,"E15")])]}),makeQuery(id+"F3.opExtrude","SWEPT_FACE",FACE,{"disambiguationData":[OSD([sQuery(id+"F2.wireOp",EDGE,"E16")])]})])],"derivedFrom":makeQuery(id+"F1.opRevolve","SWEPT_EDGE",EDGE,{"disambiguationData":[OSD([subQ0,subQ1])]})});}
            var Q14;
            Q14=makeQuery(id+"F1.opRevolve","SWEPT_EDGE",EDGE,{"disambiguationData":[OSD([sQuery(id+"F0.wireOp",EDGE,"E5"),sQuery(id+"F0.wireOp",EDGE,"E11")])]});
            var Q15;
            Q15=makeQuery(id+"F1.opRevolve","SWEPT_EDGE",EDGE,{"disambiguationData":[OSD([sQuery(id+"F0.wireOp",EDGE,"E3.top"),sQuery(id+"F0.wireOp",EDGE,"E3.right")])]});
            var Q16;
            Q16=makeQuery(id+"F3.boolean.opBoolean","COPY",EDGE,{"derivedFrom":makeQuery(id+"F3.opExtrude","CAP_EDGE",EDGE,{"disambiguationData":[OSD([sQuery(id+"F2.wireOp",EDGE,"E27")])],"isStart":true})});
            var Q17;
            Q17=makeQuery(id+"F3.boolean.opBoolean","COPY",EDGE,{"derivedFrom":makeQuery(id+"F3.opExtrude","CAP_EDGE",EDGE,{"disambiguationData":[OSD([sQuery(id+"F2.wireOp",EDGE,"E17")])],"isStart":true})});
            var Q18;
            Q18=makeQuery(id+"F3.boolean.opBoolean","COPY",EDGE,{"derivedFrom":makeQuery(id+"F3.opExtrude","CAP_EDGE",EDGE,{"disambiguationData":[OSD([sQuery(id+"F2.wireOp",EDGE,"E26")])],"isStart":true})});
            var Q19;
            Q19=makeQuery(id+"F3.boolean.opBoolean","COPY",EDGE,{"derivedFrom":makeQuery(id+"F3.opExtrude","CAP_EDGE",EDGE,{"disambiguationData":[OSD([sQuery(id+"F2.wireOp",EDGE,"E25")])],"isStart":true})});
            var Q20;
            Q20=makeQuery(id+"F3.boolean.opBoolean","COPY",EDGE,{"derivedFrom":makeQuery(id+"F3.opExtrude","CAP_EDGE",EDGE,{"disambiguationData":[OSD([sQuery(id+"F2.wireOp",EDGE,"E24")])],"isStart":true})});
            var Q21;
            Q21=makeQuery(id+"F3.boolean.opBoolean","COPY",EDGE,{"derivedFrom":makeQuery(id+"F3.opExtrude","CAP_EDGE",EDGE,{"disambiguationData":[OSD([sQuery(id+"F2.wireOp",EDGE,"E23")])],"isStart":true})});
            var Q22;
            Q22=makeQuery(id+"F3.boolean.opBoolean","COPY",EDGE,{"derivedFrom":makeQuery(id+"F3.opExtrude","CAP_EDGE",EDGE,{"disambiguationData":[OSD([sQuery(id+"F2.wireOp",EDGE,"E22")])],"isStart":true})});
            var Q23;
            Q23=makeQuery(id+"F3.boolean.opBoolean","COPY",EDGE,{"derivedFrom":makeQuery(id+"F3.opExtrude","CAP_EDGE",EDGE,{"disambiguationData":[OSD([sQuery(id+"F2.wireOp",EDGE,"E19")])],"isStart":true})});
            var Q24;
            Q24=makeQuery(id+"F3.boolean.opBoolean","COPY",EDGE,{"derivedFrom":makeQuery(id+"F3.opExtrude","CAP_EDGE",EDGE,{"disambiguationData":[OSD([sQuery(id+"F2.wireOp",EDGE,"E18")])],"isStart":true})});
            var Q25;
            Q25=makeQuery(id+"F3.boolean.opBoolean","COPY",EDGE,{"derivedFrom":makeQuery(id+"F3.opExtrude","CAP_EDGE",EDGE,{"disambiguationData":[OSD([sQuery(id+"F2.wireOp",EDGE,"E20")])],"isStart":true})});
            var Q26;
            Q26=makeQuery(id+"F3.boolean.opBoolean","COPY",EDGE,{"derivedFrom":makeQuery(id+"F3.opExtrude","CAP_EDGE",EDGE,{"disambiguationData":[OSD([sQuery(id+"F2.wireOp",EDGE,"E16")])],"isStart":true})});
            var Q27;
            Q27=makeQuery(id+"F3.boolean.opBoolean","COPY",EDGE,{"derivedFrom":makeQuery(id+"F3.opExtrude","CAP_EDGE",EDGE,{"disambiguationData":[OSD([sQuery(id+"F2.wireOp",EDGE,"E15")])],"isStart":true})});
            var Q28;
            Q28=makeQuery(id+"F3.boolean.opBoolean","COPY",EDGE,{"derivedFrom":makeQuery(id+"F3.opExtrude","CAP_EDGE",EDGE,{"disambiguationData":[OSD([sQuery(id+"F2.wireOp",EDGE,"E14")])],"isStart":true})});
            var Q29;
            Q29=makeQuery(id+"F3.boolean.opBoolean","COPY",EDGE,{"derivedFrom":makeQuery(id+"F3.opExtrude","CAP_EDGE",EDGE,{"disambiguationData":[OSD([sQuery(id+"F2.wireOp",EDGE,"E21")])],"isStart":true})});
            fillet(context, id + "F4", {"entities" : qUnion([Q0, Q1, Q2, Q3, Q4, Q5, Q6, Q7, Q8, Q9, Q10, Q11, Q12, Q13, Q14, Q15, Q16, Q17, Q18, Q19, Q20, Q21, Q22, Q23, Q24, Q25, Q26, Q27, Q28, Q29]), "radius" : 1.5 * mm, "tangentPropagation" : true, "allowEdgeOverflow" : false});
        }
    });
